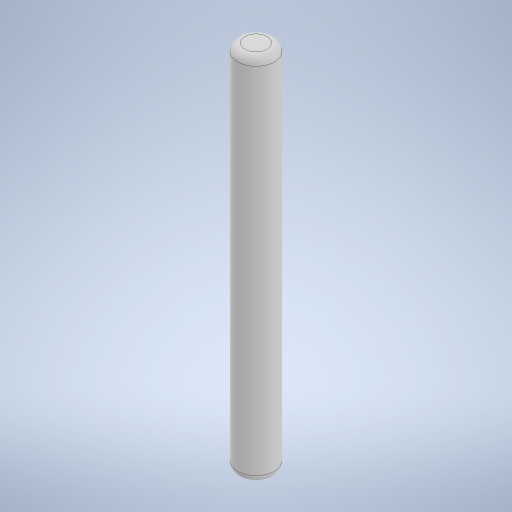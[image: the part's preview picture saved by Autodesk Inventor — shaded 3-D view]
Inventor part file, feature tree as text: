
AUTODESK INVENTOR PART (.ipt)
format: ipt  version: 2023 (Build 270158030, 158C)  size: 235,520 bytes
history: native  units: mm
features: extrude x1, fillet x1, sketch x1
ambient origin geometry x8: Origin, YZ Plane, XZ Plane, XY Plane, X Axis, Y Axis, Z Axis, Center Point
bodies: Solid1 (feature_tree)
feature tree (3):
  extrude  "Extrusion1"  Depth=50.0mm TaperAngle=0.0deg
  fillet  "Fillet1"  Radius=1.0mm
  sketch  "Sketch1"  dims[d0=5.0mm d1=50.0mm d2=0.0mm d3=1.0mm]
